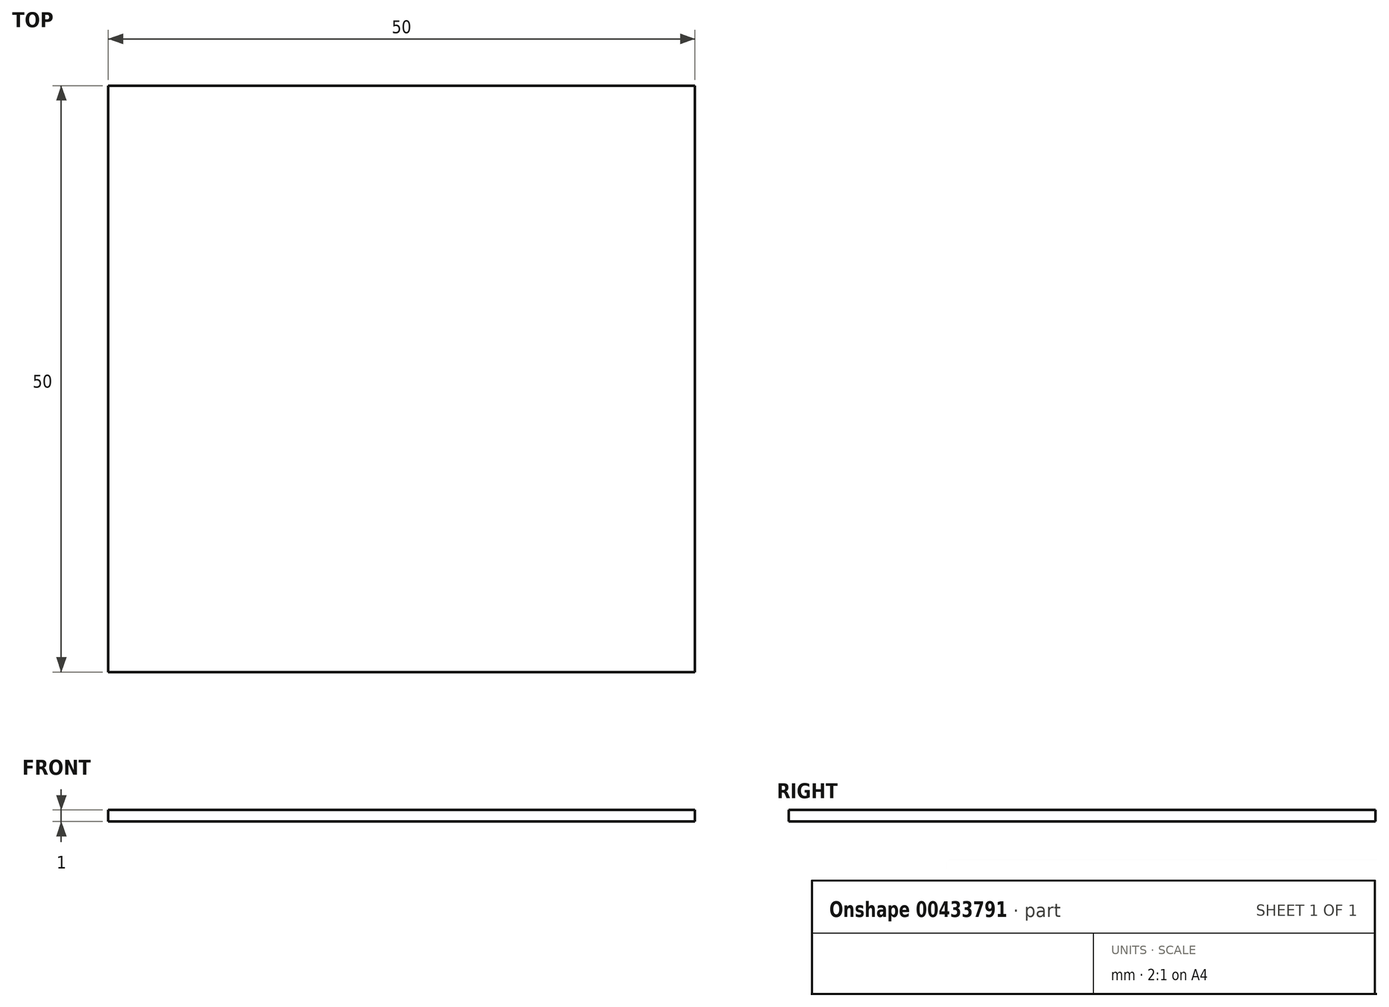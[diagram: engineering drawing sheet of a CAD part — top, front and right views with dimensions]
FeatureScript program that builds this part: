
annotation { "Feature Type Name" : "Feature", "Feature Type Description" : "" }
export const myFeature = defineFeature(function(context is Context, id is Id, definition is map)
    precondition{}
    {
        {
            var Q0;
            Q0=qCreatedBy(makeId("Top.planeOp"),FACE);
            var sketch = newSketch(context, id + "F0", { "sketchPlane" : qUnion([Q0])});
            skLineSegment(sketch, "E0.bottom", {"start": v(25, 25) * mm, "end": v(-25, 25) * mm});
            skLineSegment(sketch, "E0.top", {"start": v(25, -25) * mm, "end": v(-25, -25) * mm});
            skLineSegment(sketch, "E0.left", {"start": v(25, 25) * mm, "end": v(25, -25) * mm});
            skLineSegment(sketch, "E0.right", {"start": v(-25, 25) * mm, "end": v(-25, -25) * mm});
            skPoint(sketch, "E0.middle", {"position": v(0, 0) * mm});
            skSolve(sketch);
        }
        {
            var Q0;
            Q0=makeQuery(id+"F0.imprint","IMPRINT",FACE,{"disambiguationData":[TD([[makeQuery(id+"F0.imprint","IMPRINT",EDGE,{"derivedFrom":sQuery(id+"F0.wireOp",EDGE,"E0.bottom")}),1.0]])]});
            extrude(context, id + "F1", {"entities" : qUnion([Q0]), "depth" : 1 * mm});
        }
    });
